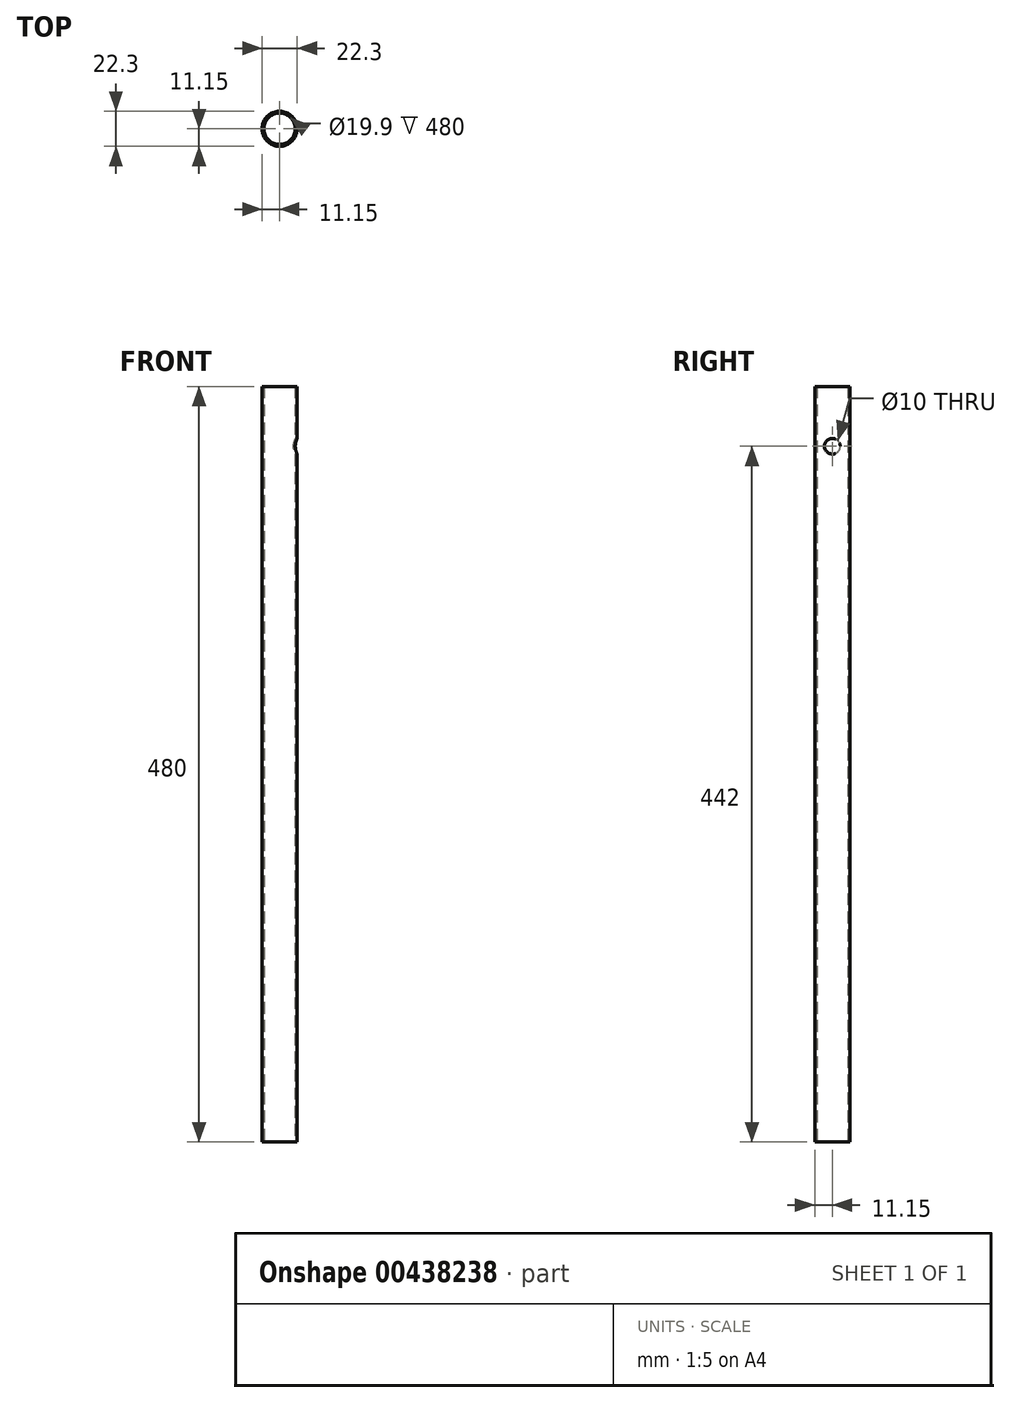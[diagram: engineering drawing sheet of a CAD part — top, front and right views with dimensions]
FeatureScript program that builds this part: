
annotation { "Feature Type Name" : "Feature", "Feature Type Description" : "" }
export const myFeature = defineFeature(function(context is Context, id is Id, definition is map)
    precondition{}
    {
        {
            var Q0;
            Q0=qCreatedBy(makeId("Top.planeOp"),FACE);
            var sketch = newSketch(context, id + "F0", { "sketchPlane" : qUnion([Q0])});
            skCircle(sketch, "E0", {"center": v(0, 0) * mm, "radius": 11.15 * mm});
            skCircle(sketch, "E1.0", {"center": v(0, 0) * mm, "radius": 9.95 * mm});
            skSolve(sketch);
        }
        {
            var Q0;
            Q0 = qSketchRegion(id + "F0", true);
            extrude(context, id + "F1", {"entities" : qUnion([Q0]), "depth" : 480 * mm});
        }
        {
            var Q0;
            Q0=qCreatedBy(makeId("Right.planeOp"),FACE);
            var sketch = newSketch(context, id + "F2", { "sketchPlane" : qUnion([Q0])});
            skCircle(sketch, "E2", {"center": v(0, 442) * mm, "radius": 5 * mm});
            skSolve(sketch);
        }
        {
            var Q0;
            Q0 = qSketchRegion(id + "F2", true);
            extrude(context, id + "F3", {"entities" : qUnion([Q0]), "operationType" : NewBodyOperationType.REMOVE, "endBound" : BoundingType.THROUGH_ALL, "depth" : 25 * mm});
        }
    });
